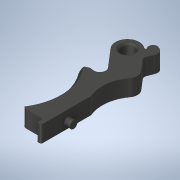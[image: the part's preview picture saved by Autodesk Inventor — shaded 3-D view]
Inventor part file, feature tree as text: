
AUTODESK INVENTOR PART (.ipt)
format: ipt  version: 2020.1 (Build 241239000, 239)  size: 345,088 bytes
history: native  units: mm
features: sketch x4, extrude x3, fillet x2, other x2, plane x1, revolve x1, mirror x1, chamfer x1
ambient origin geometry x8: Origin, YZ Plane, XZ Plane, XY Plane, X Axis, Y Axis, Z Axis, Center Point
bodies: Solid1 (feature_tree)
feature tree (15):
  extrude  "Extrusion1"  Depth=15.0mm
  plane  "Work Plane1"
  revolve  "Revolution1"  [1 undecoded]
  mirror  "Mirror1"
  chamfer  "Chamfer1"  Distance=3.0mm
  fillet  "Fillet1"  Radius=12.0mm
  fillet  "Fillet2"  Radius=3.0mm
  extrude  "Extrusion2"  Depth=1.5mm
  extrude  "Extrusion3"  Depth=0.2mm
  sketch  "Sketch1"  dims[d5=7.0mm d6=15.0mm]
  other  "Image1"
  other  "Work Axis1"
  sketch  "Sketch2"  dims[d7=8.0mm d8=4.4mm]
  sketch  "Sketch3"  dims[d9=2.0mm]
  sketch  "Sketch4"  dims[d10=35.0mm d14=3.0mm d18=12.0mm d93=3.0mm d94=1.5mm d96=3.839724mm d97=5.6mm d98=0.0mm d99=90.0deg d101=1.0mm d103=0.5mm d104=90.0deg d105=90.0deg d106=0.5mm d107=2.0mm d108=45.0deg d109=0.5mm d110=1.25mm d115=0.7mm d116=150.0deg d121=0.5mm d123=1.5mm d124=2.0mm d125=0.5mm d140=1.5mm d141=2.0mm d149=2.5mm d151=8.0mm d152=2.0mm d153=0.0mm d154=2.15mm d155=0.2mm d156=0.0mm]
note: 1 required parameter value undecoded (feature->parameter linkage not recoverable at this tier; creation-order binding heuristic only, values carry confidence <= 0.55)
